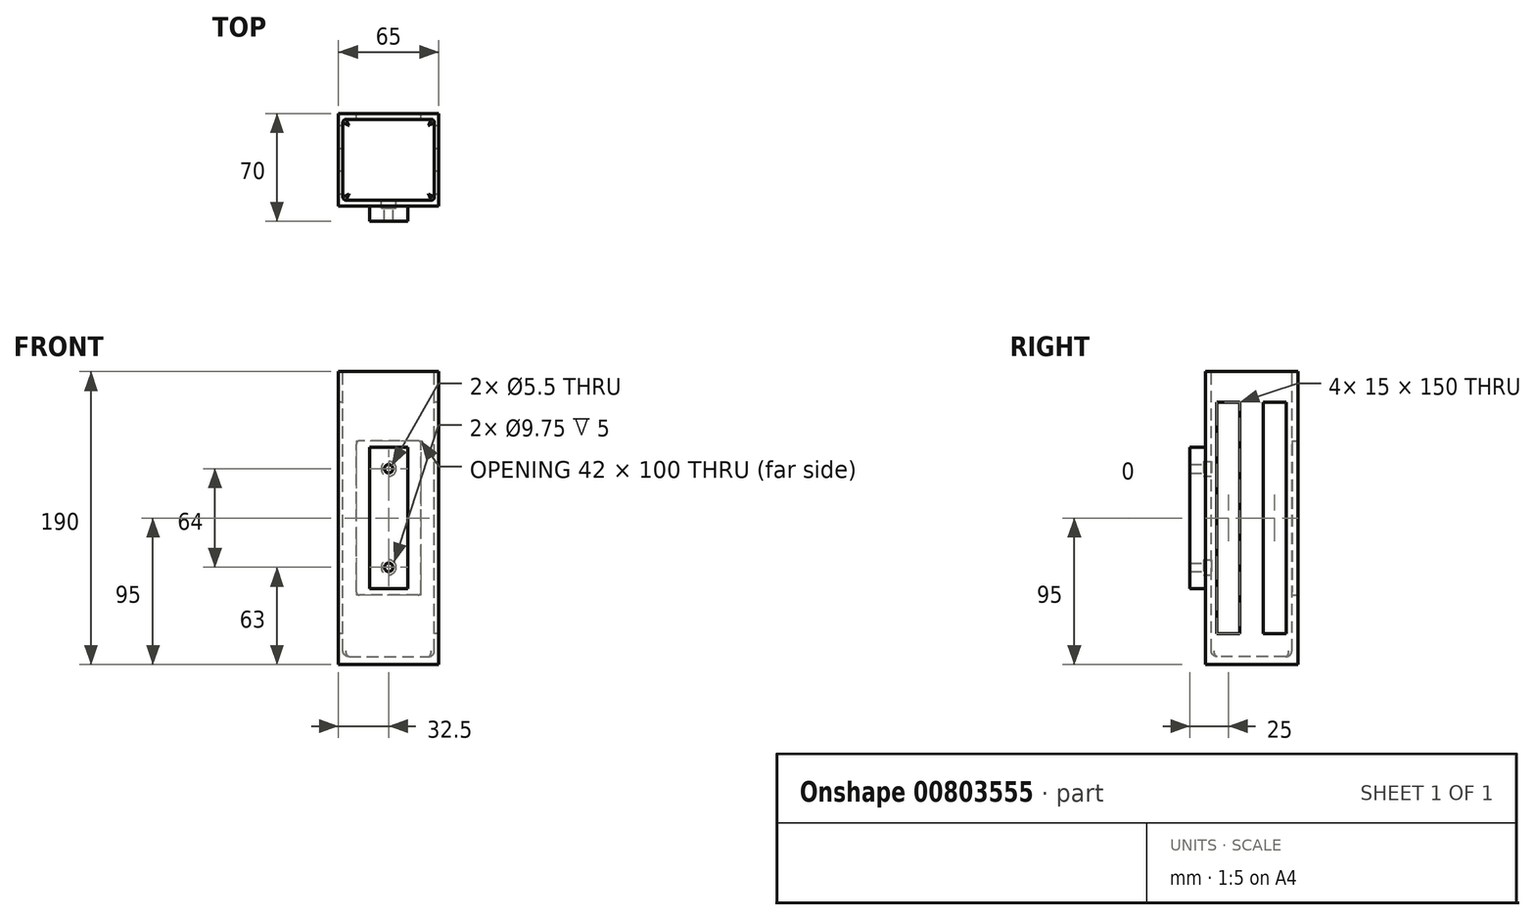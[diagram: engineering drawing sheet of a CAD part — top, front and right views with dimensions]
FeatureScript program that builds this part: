
annotation { "Feature Type Name" : "Feature", "Feature Type Description" : "" }
export const myFeature = defineFeature(function(context is Context, id is Id, definition is map)
    precondition{}
    {
        {
            var Q0;
            Q0=qCreatedBy(makeId("Top.planeOp"),FACE);
            var sketch = newSketch(context, id + "F0", { "sketchPlane" : qUnion([Q0])});
            skLineSegment(sketch, "E0.bottom", {"start": v(-32.5, 30) * mm, "end": v(32.5, 30) * mm});
            skLineSegment(sketch, "E0.top", {"start": v(-32.5, -30) * mm, "end": v(32.5, -30) * mm});
            skLineSegment(sketch, "E0.left", {"start": v(-32.5, 30) * mm, "end": v(-32.5, -30) * mm});
            skLineSegment(sketch, "E0.right", {"start": v(32.5, 30) * mm, "end": v(32.5, -30) * mm});
            skPoint(sketch, "E0.middle", {"position": v(0, 0) * mm});
            skSolve(sketch);
        }
        {
            var Q0;
            Q0=qSketchRegion(id+"F0",true);
            extrude(context, id + "F1", {"entities" : qUnion([Q0]), "depth" : 190 * mm, "offsetDistance" : 25 * mm});
        }
        {
            var Q0;
            Q0=makeQuery(id+"F1.opExtrude","CAP_FACE",FACE,{"disambiguationData":[OSD([sQuery(id+"F0.wireOp",EDGE,"E0.bottom"),sQuery(id+"F0.wireOp",EDGE,"E0.top"),sQuery(id+"F0.wireOp",EDGE,"E0.left"),sQuery(id+"F0.wireOp",EDGE,"E0.right")])],"isStart":false});
            var sketch = newSketch(context, id + "F2", { "sketchPlane" : qUnion([Q0])});
            skLineSegment(sketch, "E1.bottom", {"start": v(-29.7, 26.2) * mm, "end": v(29.7, 26.2) * mm});
            skLineSegment(sketch, "E1.top", {"start": v(-29.7, -26.2) * mm, "end": v(29.7, -26.2) * mm});
            skLineSegment(sketch, "E1.left", {"start": v(-29.7, 26.2) * mm, "end": v(-29.7, -26.2) * mm});
            skLineSegment(sketch, "E1.right", {"start": v(29.7, 26.2) * mm, "end": v(29.7, -26.2) * mm});
            skPoint(sketch, "E1.middle", {"position": v(0, 0) * mm});
            skSolve(sketch);
        }
        {
            var Q0;
            Q0=qSketchRegion(id+"F2",true);
            extrude(context, id + "F3", {"entities" : qUnion([Q0]), "operationType" : NewBodyOperationType.REMOVE, "oppositeDirection" : true, "depth" : 185 * mm, "offsetDistance" : 25 * mm});
        }
        {
            var Q0;
            Q0=makeQuery(id+"F1.opExtrude","SWEPT_FACE",FACE,{"disambiguationData":[OSD([sQuery(id+"F0.wireOp",EDGE,"E0.bottom")])]});
            var sketch = newSketch(context, id + "F4", { "sketchPlane" : qUnion([Q0])});
            skLineSegment(sketch, "E2.bottom", {"start": v(-21, 45) * mm, "end": v(21, 45) * mm});
            skLineSegment(sketch, "E2.top", {"start": v(-21, 145) * mm, "end": v(21, 145) * mm});
            skLineSegment(sketch, "E2.left", {"start": v(-21, 45) * mm, "end": v(-21, 145) * mm});
            skLineSegment(sketch, "E2.right", {"start": v(21, 45) * mm, "end": v(21, 145) * mm});
            skPoint(sketch, "E2.middle", {"position": v(0, 95) * mm});
            skPoint(sketch, "E2.middle.positionSnap0", {"position": v(-32.5, 95) * mm});
            skPoint(sketch, "E2.middle.positionSnap1", {"position": v(0, 0) * mm});
            skPoint(sketch, "E2.centerSnap0", {"position": v(-32.5, 95) * mm});
            skPoint(sketch, "E2.centerSnap1", {"position": v(0, 0) * mm});
            skSolve(sketch);
        }
        {
            var Q0;
            Q0=qSketchRegion(id+"F4",true);
            extrude(context, id + "F5", {"entities" : qUnion([Q0]), "operationType" : NewBodyOperationType.REMOVE, "oppositeDirection" : true, "depth" : 20 * mm, "offsetDistance" : 25 * mm});
        }
        {
            var Q0;
            Q0=makeQuery(id+"F5.boolean.opBoolean","COPY",EDGE,{"derivedFrom":makeQuery(id+"F5.opExtrude","SWEPT_EDGE",EDGE,{"disambiguationData":[OSD([sQuery(id+"F4.wireOp",EDGE,"E2.bottom"),sQuery(id+"F4.wireOp",EDGE,"E2.left")])]})});
            var Q1;
            Q1=makeQuery(id+"F5.boolean.opBoolean","COPY",EDGE,{"derivedFrom":makeQuery(id+"F5.opExtrude","SWEPT_EDGE",EDGE,{"disambiguationData":[OSD([sQuery(id+"F4.wireOp",EDGE,"E2.bottom"),sQuery(id+"F4.wireOp",EDGE,"E2.right")])]})});
            var Q2;
            Q2=makeQuery(id+"F5.boolean.opBoolean","COPY",EDGE,{"derivedFrom":makeQuery(id+"F5.opExtrude","SWEPT_EDGE",EDGE,{"disambiguationData":[OSD([sQuery(id+"F4.wireOp",EDGE,"E2.top"),sQuery(id+"F4.wireOp",EDGE,"E2.right")])]})});
            var Q3;
            Q3=makeQuery(id+"F5.boolean.opBoolean","COPY",EDGE,{"derivedFrom":makeQuery(id+"F5.opExtrude","SWEPT_EDGE",EDGE,{"disambiguationData":[OSD([sQuery(id+"F4.wireOp",EDGE,"E2.top"),sQuery(id+"F4.wireOp",EDGE,"E2.left")])]})});
            fillet(context, id + "F6", {"entities" : qUnion([Q0, Q1, Q2, Q3]), "radius" : 2 * mm, "tangentPropagation" : true, "allowEdgeOverflow" : false});
        }
        {
            var Q0;
            Q0=makeQuery(id+"F3.boolean.opBoolean","COPY",EDGE,{"derivedFrom":makeQuery(id+"F3.opExtrude","CAP_EDGE",EDGE,{"disambiguationData":[OSD([sQuery(id+"F2.wireOp",EDGE,"E1.right")])],"isStart":false})});
            var Q1;
            Q1=makeQuery(id+"F3.boolean.opBoolean","COPY",EDGE,{"derivedFrom":makeQuery(id+"F3.opExtrude","CAP_EDGE",EDGE,{"disambiguationData":[OSD([sQuery(id+"F2.wireOp",EDGE,"E1.top")])],"isStart":false})});
            var Q2;
            Q2=makeQuery(id+"F3.boolean.opBoolean","COPY",EDGE,{"derivedFrom":makeQuery(id+"F3.opExtrude","CAP_EDGE",EDGE,{"disambiguationData":[OSD([sQuery(id+"F2.wireOp",EDGE,"E1.left")])],"isStart":false})});
            var Q3;
            Q3=makeQuery(id+"F3.boolean.opBoolean","COPY",EDGE,{"derivedFrom":makeQuery(id+"F3.opExtrude","CAP_EDGE",EDGE,{"disambiguationData":[OSD([sQuery(id+"F2.wireOp",EDGE,"E1.bottom")])],"isStart":false})});
            fillet(context, id + "F7", {"entities" : qUnion([Q0, Q1, Q2, Q3]), "radius" : 4 * mm, "tangentPropagation" : true, "allowEdgeOverflow" : false});
        }
        {
            var Q0;
            Q0=makeQuery(id+"F3.boolean.opBoolean","COPY",EDGE,{"derivedFrom":makeQuery(id+"F3.opExtrude","SWEPT_EDGE",EDGE,{"disambiguationData":[OSD([sQuery(id+"F2.wireOp",EDGE,"E1.top"),sQuery(id+"F2.wireOp",EDGE,"E1.right")])]})});
            var Q1;
            Q1=makeQuery(id+"F3.boolean.opBoolean","COPY",EDGE,{"derivedFrom":makeQuery(id+"F3.opExtrude","SWEPT_EDGE",EDGE,{"disambiguationData":[OSD([sQuery(id+"F2.wireOp",EDGE,"E1.bottom"),sQuery(id+"F2.wireOp",EDGE,"E1.right")])]})});
            var Q2;
            Q2=makeQuery(id+"F3.boolean.opBoolean","COPY",EDGE,{"derivedFrom":makeQuery(id+"F3.opExtrude","SWEPT_EDGE",EDGE,{"disambiguationData":[OSD([sQuery(id+"F2.wireOp",EDGE,"E1.top"),sQuery(id+"F2.wireOp",EDGE,"E1.left")])]})});
            var Q3;
            Q3=makeQuery(id+"F3.boolean.opBoolean","COPY",EDGE,{"derivedFrom":makeQuery(id+"F3.opExtrude","SWEPT_EDGE",EDGE,{"disambiguationData":[OSD([sQuery(id+"F2.wireOp",EDGE,"E1.bottom"),sQuery(id+"F2.wireOp",EDGE,"E1.left")])]})});
            fillet(context, id + "F8", {"entities" : qUnion([Q0, Q1, Q2, Q3]), "radius" : 2 * mm, "tangentPropagation" : true, "allowEdgeOverflow" : false});
        }
        {
            var Q0;
            Q0=makeQuery(id+"F1.opExtrude","SWEPT_FACE",FACE,{"disambiguationData":[OSD([sQuery(id+"F0.wireOp",EDGE,"E0.left")])]});
            var sketch = newSketch(context, id + "F9", { "sketchPlane" : qUnion([Q0])});
            skLineSegment(sketch, "E3", {"start": v(0, 0) * mm, "end": v(-30, 0) * mm});
            skLineSegment(sketch, "E4", {"start": v(0, 0) * mm, "end": v(30, 0) * mm});
            skLineSegment(sketch, "E5.bottom", {"start": v(22.5, 20) * mm, "end": v(7.5, 20) * mm});
            skLineSegment(sketch, "E5.top", {"start": v(22.5, 170) * mm, "end": v(7.5, 170) * mm});
            skLineSegment(sketch, "E5.left", {"start": v(22.5, 20) * mm, "end": v(22.5, 170) * mm});
            skLineSegment(sketch, "E5.right", {"start": v(7.5, 20) * mm, "end": v(7.5, 170) * mm});
            skPoint(sketch, "E5.middle", {"position": v(15, 95) * mm});
            skPoint(sketch, "E5.middle.positionSnap0", {"position": v(30, 95) * mm});
            skPoint(sketch, "E5.middle.positionSnap1", {"position": v(15, 0) * mm});
            skPoint(sketch, "E5.centerSnap0", {"position": v(30, 95) * mm});
            skPoint(sketch, "E5.centerSnap1", {"position": v(15, 0) * mm});
            skSolve(sketch);
        }
        {
            var Q0;
            Q0=makeQuery(id+"F9.imprint","IMPRINT",FACE,{"disambiguationData":[TD([[makeQuery(id+"F9.imprint","IMPRINT",EDGE,{"derivedFrom":sQuery(id+"F9.wireOp",EDGE,"E5.bottom")}),-1.0]])]});
            extrude(context, id + "F10", {"entities" : qUnion([Q0]), "operationType" : NewBodyOperationType.REMOVE, "oppositeDirection" : true, "depth" : 400 * mm, "offsetDistance" : 25 * mm});
        }
        {
            var Q0;
            Q0=makeQuery(id+"F1.opExtrude","SWEPT_FACE",FACE,{"disambiguationData":[OSD([sQuery(id+"F0.wireOp",EDGE,"E0.right")])]});
            var sketch = newSketch(context, id + "F11", { "sketchPlane" : qUnion([Q0])});
            skLineSegment(sketch, "E6.bottom", {"start": v(7.5, 170) * mm, "end": v(22.5, 170) * mm});
            skLineSegment(sketch, "E6.top", {"start": v(7.5, 20) * mm, "end": v(22.5, 20) * mm});
            skLineSegment(sketch, "E6.left", {"start": v(7.5, 170) * mm, "end": v(7.5, 20) * mm});
            skLineSegment(sketch, "E6.right", {"start": v(22.5, 170) * mm, "end": v(22.5, 20) * mm});
            skPoint(sketch, "E6.middle", {"position": v(15, 95) * mm});
            skPoint(sketch, "E6.middle.positionSnap0", {"position": v(30, 95) * mm});
            skPoint(sketch, "E6.centerSnap0", {"position": v(30, 95) * mm});
            skSolve(sketch);
        }
        {
            var Q0;
            Q0=qSketchRegion(id+"F11",true);
            extrude(context, id + "F12", {"entities" : qUnion([Q0]), "operationType" : NewBodyOperationType.REMOVE, "oppositeDirection" : true, "depth" : 400 * mm, "offsetDistance" : 25 * mm});
        }
        {
            var Q0;
            Q0=makeQuery(id+"F1.opExtrude","SWEPT_FACE",FACE,{"disambiguationData":[OSD([sQuery(id+"F0.wireOp",EDGE,"E0.top")])]});
            var sketch = newSketch(context, id + "F13", { "sketchPlane" : qUnion([Q0])});
            skLineSegment(sketch, "E7.bottom", {"start": v(-12.47, 140.93) * mm, "end": v(12.47, 140.93) * mm});
            skLineSegment(sketch, "E7.top", {"start": v(-12.47, 49.07) * mm, "end": v(12.47, 49.07) * mm});
            skLineSegment(sketch, "E7.left", {"start": v(-12.47, 140.93) * mm, "end": v(-12.47, 49.07) * mm});
            skLineSegment(sketch, "E7.right", {"start": v(12.47, 140.93) * mm, "end": v(12.47, 49.07) * mm});
            skPoint(sketch, "E7.middle", {"position": v(0, 95) * mm});
            skPoint(sketch, "E7.middle.positionSnap0", {"position": v(-32.5, 95) * mm});
            skPoint(sketch, "E7.centerSnap0", {"position": v(-32.5, 95) * mm});
            skSolve(sketch);
        }
        {
            var Q0;
            Q0=qSketchRegion(id+"F13",true);
            extrude(context, id + "F14", {"entities" : qUnion([Q0]), "operationType" : NewBodyOperationType.ADD, "depth" : 10 * mm, "offsetDistance" : 25 * mm});
        }
        {
            var Q0;
            Q0=makeQuery(id+"F3.boolean.opBoolean","COPY",FACE,{"derivedFrom":makeQuery(id+"F3.opExtrude","SWEPT_FACE",FACE,{"disambiguationData":[OSD([sQuery(id+"F2.wireOp",EDGE,"E1.top")])]})});
            var sketch = newSketch(context, id + "F15", { "sketchPlane" : qUnion([Q0])});
            skLineSegment(sketch, "E8", {"start": v(0, 95) * mm, "end": v(0, 63) * mm});
            skLineSegment(sketch, "E9", {"start": v(0, 95) * mm, "end": v(0, 127) * mm});
            skSolve(sketch);
        }
        {
            var Q0;
            Q0=sQuery(id+"F15.wireOp",VERTEX,"E9.end");
            var Q1;
            Q1=sQuery(id+"F15.wireOp",VERTEX,"E8.end");
            var Q2;
            Q2=makeQuery(id+"F1.opExtrude","SWEPT_BODY",BODY,{"disambiguationData":[OSD([sQuery(id+"F0.wireOp",EDGE,"E0.bottom"),sQuery(id+"F0.wireOp",EDGE,"E0.top"),sQuery(id+"F0.wireOp",EDGE,"E0.left"),sQuery(id+"F0.wireOp",EDGE,"E0.right")])]});
            hole(context, id + "F16", {"style" : HoleStyle.C_BORE, "endStyle" : HoleEndStyle.THROUGH, "standardTappedOrClearance" : lookupTablePath({ "fit" : "Normal", "standard" : "ISO", "size" : "M5", "type" : "Clearance" }), "standardBlindInLast" : lookupTablePath({ "fit" : "Standard", "standard" : "ISO", "size" : "M5", "type" : "Clearance" }), "holeDiameter" : 5.5 * mm, "cBoreDiameter" : 9.75 * mm, "cBoreDepth" : 5 * mm, "majorDiameter" : 10 * mm, "isTappedThrough" : true, "tappedDepth" : 20 * mm, "tapClearance" : 3, "locations" : qUnion([Q0, Q1]), "scope" : qUnion([Q2])});
        }
    });
